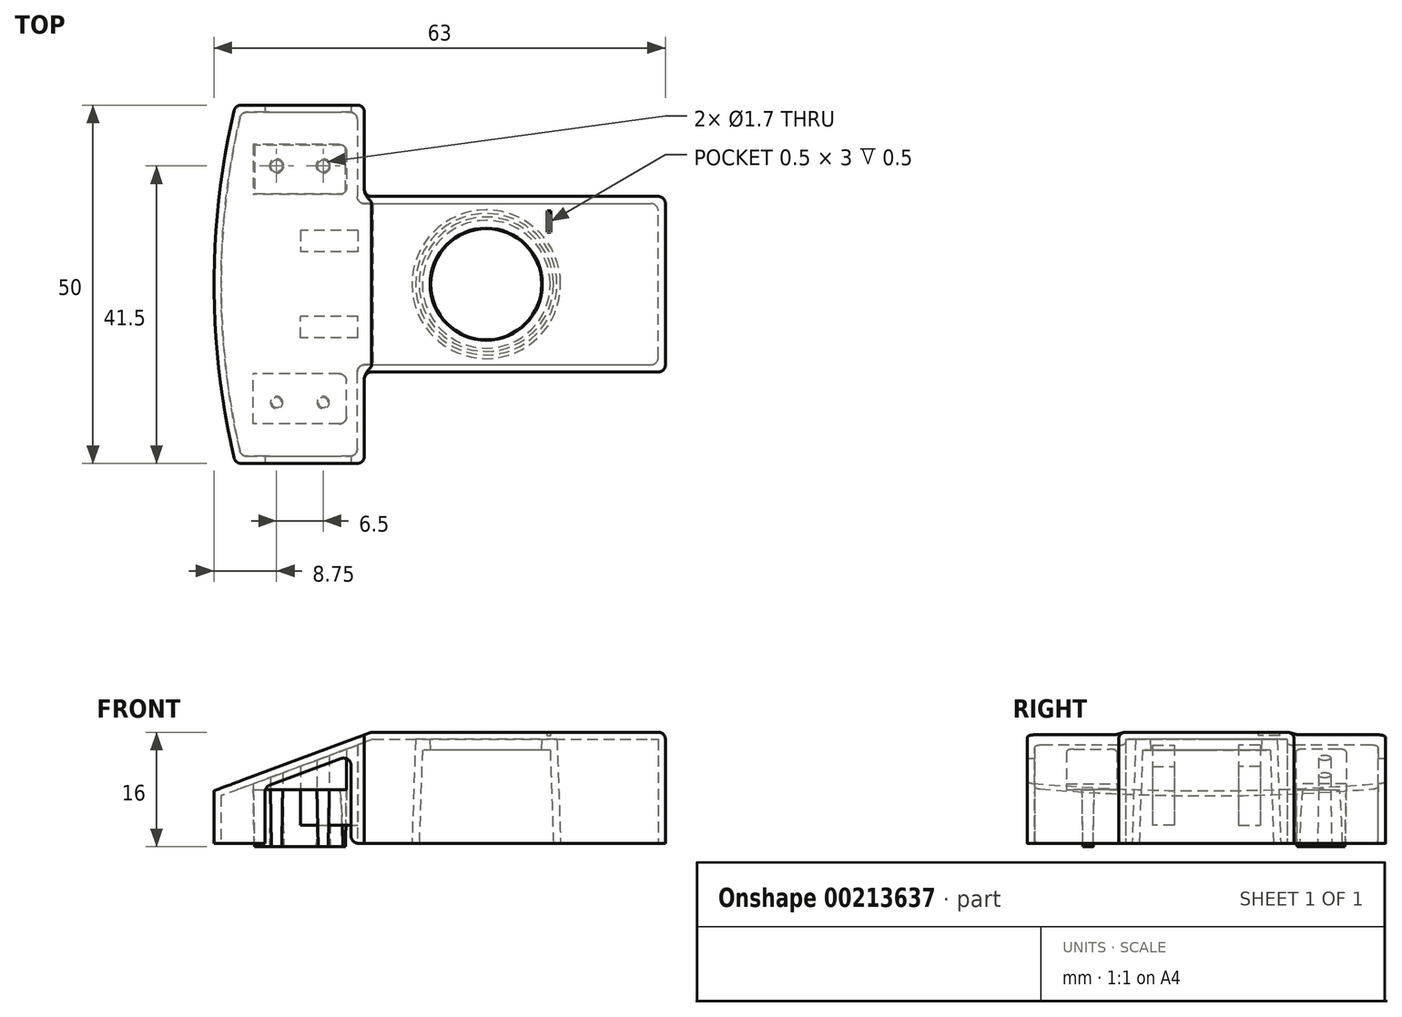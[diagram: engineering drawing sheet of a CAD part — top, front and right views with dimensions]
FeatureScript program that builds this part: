
annotation { "Feature Type Name" : "Feature", "Feature Type Description" : "" }
export const myFeature = defineFeature(function(context is Context, id is Id, definition is map)
    precondition{}
    {
        {
            var Q0;
            Q0=qCreatedBy(makeId("Top.planeOp"),FACE);
            var sketch = newSketch(context, id + "F0", { "sketchPlane" : qUnion([Q0])});
            skCircle(sketch, "E0", {"center": v(-4, 0) * mm, "radius": 9.37 * mm});
            skLineSegment(sketch, "E1.bottom", {"start": v(-21, -12.25) * mm, "end": v(21, -12.25) * mm});
            skLineSegment(sketch, "E1.top", {"start": v(-21, 12.25) * mm, "end": v(21, 12.25) * mm});
            skLineSegment(sketch, "E1.right", {"start": v(21, -12.25) * mm, "end": v(21, 12.25) * mm});
            skLineSegment(sketch, "E2.bottom", {"start": v(-21, -25) * mm, "end": v(-39, -25) * mm});
            skLineSegment(sketch, "E2.top", {"start": v(-21, 25) * mm, "end": v(-39, 25) * mm});
            skLineSegment(sketch, "E2.left", {"start": v(-21, -25) * mm, "end": v(-21, -12.25) * mm});
            skLineSegment(sketch, "E2.right", {"start": v(-39, -25) * mm, "end": v(-39, 25) * mm});
            skPoint(sketch, "E2.middle", {"position": v(-30, 0) * mm});
            skLineSegment(sketch, "E3.trimOffspring", {"start": v(-21, 12.25) * mm, "end": v(-21, 25) * mm});
            skLineSegment(sketch, "E4", {"start": v(-20, 12.25) * mm, "end": v(-20, -12.25) * mm});
            skPoint(sketch, "E5", {"position": v(-42, 0) * mm});
            skPoint(sketch, "E5.positionSnap0", {"position": v(-39, 0) * mm});
            skArc(sketch, "E6", {"start": v(-39, 25) * mm, "mid": v(-42, 0) * mm, "end": v(-39, -25) * mm});
            skSolve(sketch);
        }
        {
            var Q0;
            Q0=qSketchRegion(id+"F0",true);
            var Q1;
            Q1=makeQuery(id+"F0.imprint","IMPRINT",FACE,{"disambiguationData":[TD([[makeQuery(id+"F0.imprint","IMPRINT",EDGE,{"derivedFrom":sQuery(id+"F0.wireOp",EDGE,"E0")}),1.0]])]});
            extrude(context, id + "F1", {"entities" : qUnion([Q0, Q1]), "depth" : 15.5 * mm});
        }
        {
            var Q0;
            Q0=makeQuery(id+"F0.imprint","IMPRINT",FACE,{"disambiguationData":[TD([[makeQuery(id+"F0.imprint","IMPRINT",EDGE,{"derivedFrom":sQuery(id+"F0.wireOp",EDGE,"E0")}),1.0]])]});
            var Q1;
            Q1=makeQuery(id+"F1.opExtrude","CAP_FACE",FACE,{"disambiguationData":[OSD([sQuery(id+"F0.wireOp",EDGE,"E1.bottom"),sQuery(id+"F0.wireOp",EDGE,"E1.top"),sQuery(id+"F0.wireOp",EDGE,"E1.right"),sQuery(id+"F0.wireOp",EDGE,"E2.bottom"),sQuery(id+"F0.wireOp",EDGE,"E2.top"),sQuery(id+"F0.wireOp",EDGE,"E2.left"),sQuery(id+"F0.wireOp",EDGE,"E3.trimOffspring"),sQuery(id+"F0.wireOp",EDGE,"E6")])],"isStart":false});
            extrude(context, id + "F2", {"entities" : qUnion([Q0]), "operationType" : NewBodyOperationType.REMOVE, "endBound" : BoundingType.UP_TO_SURFACE, "endBoundEntityFace" : qUnion([Q1]), "depth" : 25 * mm, "hasDraft" : true, "draftAngle" : 2 * degree, "draftPullDirection" : true});
        }
        {
            var Q0;
            Q0=qCreatedBy(makeId("Front.planeOp"),FACE);
            var Q1;
            Q1=makeQuery(id+"F1.opExtrude","CAP_EDGE",EDGE,{"disambiguationData":[OSD([sQuery(id+"F0.wireOp",EDGE,"E2.bottom")])],"isStart":true});
            cPlane(context, id + "F3", {"entities" : qUnion([Q0, Q1]), "cplaneType" : CPlaneType.LINE_ANGLE, "offset" : 25 * mm, "angle" : 0 * degree, "width" : 150 * mm, "height" : 150 * mm});
        }
        {
            var Q0;
            Q0=qCreatedBy(id+"F3.planeOp",FACE);
            var sketch = newSketch(context, id + "F4", { "sketchPlane" : qUnion([Q0])});
            skLineSegment(sketch, "E7", {"start": v(20, 15.5) * mm, "end": v(42, 15.5) * mm});
            skLineSegment(sketch, "E8", {"start": v(42, 15.5) * mm, "end": v(42, 7.32) * mm});
            skLineSegment(sketch, "E9", {"start": v(42, 7.32) * mm, "end": v(20, 15.5) * mm});
            skLineSegment(sketch, "E10", {"start": v(42, 0) * mm, "end": v(41.46, 15.5) * mm, "construction": true});
            skLineSegment(sketch, "E11", {"start": v(42, 0) * mm, "end": v(42, 27.73) * mm, "construction": true});
            skSolve(sketch);
        }
        {
            var Q0;
            Q0=qSketchRegion(id+"F4",true);
            extrude(context, id + "F5", {"entities" : qUnion([Q0]), "operationType" : NewBodyOperationType.REMOVE, "endBound" : BoundingType.THROUGH_ALL, "depth" : 25 * mm});
        }
        {
            var Q0;
            Q0=makeQuery(id+"F1.opExtrude","CAP_FACE",FACE,{"disambiguationData":[OSD([sQuery(id+"F0.wireOp",EDGE,"E1.bottom"),sQuery(id+"F0.wireOp",EDGE,"E1.top"),sQuery(id+"F0.wireOp",EDGE,"E1.right"),sQuery(id+"F0.wireOp",EDGE,"E2.bottom"),sQuery(id+"F0.wireOp",EDGE,"E2.top"),sQuery(id+"F0.wireOp",EDGE,"E2.left"),sQuery(id+"F0.wireOp",EDGE,"E3.trimOffspring"),sQuery(id+"F0.wireOp",EDGE,"E6")])],"isStart":true});
            shell(context, id + "F6", {"entities" : qUnion([Q0]), "thickness" : 1 * mm});
        }
        {
            var Q0;
            Q0=makeQuery(id+"F1.opExtrude","SWEPT_FACE",FACE,{"disambiguationData":[OSD([sQuery(id+"F0.wireOp",EDGE,"E2.bottom")])]});
            var sketch = newSketch(context, id + "F7", { "sketchPlane" : qUnion([Q0])});
            skLineSegment(sketch, "E12", {"start": v(-20, 15.5) * mm, "end": v(-39, 8.43) * mm});
            skLineSegment(sketch, "E13", {"start": v(-39, 8.43) * mm, "end": v(-39, 15.5) * mm});
            skLineSegment(sketch, "E14", {"start": v(-39, 15.5) * mm, "end": v(-20, 15.5) * mm});
            skLineSegment(sketch, "E15", {"start": v(-34.87, 0) * mm, "end": v(-34.87, 7.86) * mm});
            skLineSegment(sketch, "E16", {"start": v(-34.87, 7.86) * mm, "end": v(-22.87, 12.32) * mm});
            skLineSegment(sketch, "E17", {"start": v(-22.87, 0) * mm, "end": v(-34.87, 0) * mm});
            skLineSegment(sketch, "E18", {"start": v(-22.87, 12.32) * mm, "end": v(-22.87, 0) * mm});
            skSolve(sketch);
        }
        {
            var Q0;
            Q0=makeQuery(id+"F7.imprint","IMPRINT",FACE,{"disambiguationData":[TD([[makeQuery(id+"F7.imprint","IMPRINT",EDGE,{"derivedFrom":sQuery(id+"F7.wireOp",EDGE,"E15")}),-1.0]])]});
            extrude(context, id + "F8", {"entities" : qUnion([Q0]), "operationType" : NewBodyOperationType.REMOVE, "endBound" : BoundingType.THROUGH_ALL, "oppositeDirection" : true, "depth" : 25 * mm});
        }
        {
            var Q0;
            Q0=makeQuery(id+"F1.opExtrude","CAP_FACE",FACE,{"disambiguationData":[OSD([sQuery(id+"F0.wireOp",EDGE,"E0"),sQuery(id+"F0.wireOp",EDGE,"E1.bottom"),sQuery(id+"F0.wireOp",EDGE,"E1.top"),sQuery(id+"F0.wireOp",EDGE,"E1.right"),sQuery(id+"F0.wireOp",EDGE,"E2.bottom"),sQuery(id+"F0.wireOp",EDGE,"E2.top"),sQuery(id+"F0.wireOp",EDGE,"E2.left"),sQuery(id+"F0.wireOp",EDGE,"E2.right"),sQuery(id+"F0.wireOp",EDGE,"E3.trimOffspring")])],"isStart":false});
            cPlane(context, id + "F9", {"entities" : qUnion([Q0]), "cplaneType" : CPlaneType.OFFSET, "offset" : 8 * mm, "oppositeDirection" : true, "width" : 150 * mm, "height" : 150 * mm});
        }
        {
            var Q0;
            Q0=qCreatedBy(id+"F9.planeOp",FACE);
            var sketch = newSketch(context, id + "F10", { "sketchPlane" : qUnion([Q0])});
            skLineSegment(sketch, "E19", {"start": v(0, 0) * mm, "end": v(-63, 0) * mm, "construction": true});
            skLineSegment(sketch, "E20.bottom", {"start": v(-36.5, -12.5) * mm, "end": v(-23.5, -12.5) * mm});
            skLineSegment(sketch, "E20.top", {"start": v(-36.5, -19.5) * mm, "end": v(-23.5, -19.5) * mm});
            skLineSegment(sketch, "E20.left", {"start": v(-36.5, -12.5) * mm, "end": v(-36.5, -19.5) * mm});
            skLineSegment(sketch, "E20.right", {"start": v(-23.5, -12.5) * mm, "end": v(-23.5, -19.5) * mm});
            skPoint(sketch, "E20.middle", {"position": v(-30, -16) * mm});
            skPoint(sketch, "E21", {"position": v(-33.25, -16.5) * mm});
            skPoint(sketch, "E22", {"position": v(-26.75, -16.5) * mm});
            skCircle(sketch, "E23", {"center": v(-33.25, -16.5) * mm, "radius": 0.85 * mm});
            skCircle(sketch, "E24", {"center": v(-26.75, -16.5) * mm, "radius": 0.85 * mm});
            skLineSegment(sketch, "E25.MirrorCS", {"start": v(-36.5, 12.5) * mm, "end": v(-23.5, 12.5) * mm});
            skLineSegment(sketch, "E26.MirrorCS", {"start": v(-36.5, 12.5) * mm, "end": v(-36.5, 19.5) * mm});
            skLineSegment(sketch, "E27.MirrorCS", {"start": v(-36.5, 19.5) * mm, "end": v(-23.5, 19.5) * mm});
            skLineSegment(sketch, "E28.MirrorCS", {"start": v(-23.5, 12.5) * mm, "end": v(-23.5, 19.5) * mm});
            skCircle(sketch, "E29.MirrorC", {"center": v(-26.75, 16.5) * mm, "radius": 0.85 * mm});
            skCircle(sketch, "E30.MirrorC", {"center": v(-33.25, 16.5) * mm, "radius": 0.85 * mm});
            skSolve(sketch);
        }
        {
            var Q0;
            Q0=makeQuery(id+"F10.imprint","IMPRINT",FACE,{"disambiguationData":[TD([[makeQuery(id+"F10.imprint","IMPRINT",EDGE,{"derivedFrom":sQuery(id+"F10.wireOp",EDGE,"E20.bottom")}),-1.0]])]});
            var Q1;
            Q1=makeQuery(id+"F10.imprint","IMPRINT",FACE,{"disambiguationData":[TD([[makeQuery(id+"F10.imprint","IMPRINT",EDGE,{"derivedFrom":sQuery(id+"F10.wireOp",EDGE,"E23")}),1.0]])]});
            var Q2;
            Q2=makeQuery(id+"F10.imprint","IMPRINT",FACE,{"disambiguationData":[TD([[makeQuery(id+"F10.imprint","IMPRINT",EDGE,{"derivedFrom":sQuery(id+"F10.wireOp",EDGE,"E24")}),1.0]])]});
            var Q3;
            Q3=makeQuery(id+"F10.imprint","IMPRINT",FACE,{"disambiguationData":[TD([[makeQuery(id+"F10.imprint","IMPRINT",EDGE,{"derivedFrom":sQuery(id+"F10.wireOp",EDGE,"E25.MirrorCS")}),1.0]])]});
            var Q4;
            Q4=makeQuery(id+"F10.imprint","IMPRINT",FACE,{"disambiguationData":[TD([[makeQuery(id+"F10.imprint","IMPRINT",EDGE,{"derivedFrom":sQuery(id+"F10.wireOp",EDGE,"E30.MirrorC")}),-1.0]])]});
            var Q5;
            Q5=makeQuery(id+"F10.imprint","IMPRINT",FACE,{"disambiguationData":[TD([[makeQuery(id+"F10.imprint","IMPRINT",EDGE,{"derivedFrom":sQuery(id+"F10.wireOp",EDGE,"E29.MirrorC")}),-1.0]])]});
            var Q6;
            Q6=makeQuery(id+"F6.opShell","OFFSET_FACE",FACE,{"disambiguationData":[OSD([sQuery(id+"F4.wireOp",EDGE,"E9")])]});
            extrude(context, id + "F11", {"entities" : qUnion([Q0, Q1, Q2, Q3, Q4, Q5]), "operationType" : NewBodyOperationType.ADD, "endBound" : BoundingType.UP_TO_SURFACE, "endBoundEntityFace" : qUnion([Q6]), "depth" : 25 * mm});
        }
        {
            var Q0;
            Q0=makeQuery(id+"F10.imprint","IMPRINT",FACE,{"disambiguationData":[TD([[makeQuery(id+"F10.imprint","IMPRINT",EDGE,{"derivedFrom":sQuery(id+"F10.wireOp",EDGE,"E23")}),1.0]])]});
            var Q1;
            Q1=makeQuery(id+"F10.imprint","IMPRINT",FACE,{"disambiguationData":[TD([[makeQuery(id+"F10.imprint","IMPRINT",EDGE,{"derivedFrom":sQuery(id+"F10.wireOp",EDGE,"E29.MirrorC")}),-1.0]])]});
            var Q2;
            Q2=makeQuery(id+"F10.imprint","IMPRINT",FACE,{"disambiguationData":[TD([[makeQuery(id+"F10.imprint","IMPRINT",EDGE,{"derivedFrom":sQuery(id+"F10.wireOp",EDGE,"E30.MirrorC")}),-1.0]])]});
            var Q3;
            Q3=makeQuery(id+"F10.imprint","IMPRINT",FACE,{"disambiguationData":[TD([[makeQuery(id+"F10.imprint","IMPRINT",EDGE,{"derivedFrom":sQuery(id+"F10.wireOp",EDGE,"E24")}),1.0]])]});
            extrude(context, id + "F12", {"entities" : qUnion([Q0, Q1, Q2, Q3]), "operationType" : NewBodyOperationType.ADD, "oppositeDirection" : true, "depth" : 8 * mm, "hasDraft" : true, "draftAngle" : 1 * degree, "draftPullDirection" : true});
        }
        {
            var Q0;
            Q0=makeQuery(id+"F1.opExtrude","CAP_EDGE",EDGE,{"disambiguationData":[OSD([sQuery(id+"F0.wireOp",EDGE,"E1.bottom")])],"isStart":false});
            var Q1;
            Q1=makeQuery(id+"F1.opExtrude","CAP_EDGE",EDGE,{"disambiguationData":[OSD([sQuery(id+"F0.wireOp",EDGE,"E1.right")])],"isStart":false});
            var Q2;
            Q2=makeQuery(id+"F1.opExtrude","CAP_EDGE",EDGE,{"disambiguationData":[OSD([sQuery(id+"F0.wireOp",EDGE,"E1.top")])],"isStart":false});
            var Q3;
            Q3=makeQuery(id+"F1.opExtrude","SWEPT_EDGE",EDGE,{"disambiguationData":[OSD([sQuery(id+"F0.wireOp",EDGE,"E1.bottom"),sQuery(id+"F0.wireOp",EDGE,"E1.right")])]});
            var Q4;
            Q4=makeQuery(id+"F1.opExtrude","SWEPT_EDGE",EDGE,{"disambiguationData":[OSD([sQuery(id+"F0.wireOp",EDGE,"E1.top"),sQuery(id+"F0.wireOp",EDGE,"E1.right")])]});
            fillet(context, id + "F13", {"entities" : qUnion([Q0, Q1, Q2, Q3, Q4]), "radius" : 1 * mm, "tangentPropagation" : true, "allowEdgeOverflow" : false});
        }
        {
            var Q0;
            Q0=makeQuery(id+"F1.opExtrude","SWEPT_EDGE",EDGE,{"disambiguationData":[OSD([sQuery(id+"F0.wireOp",EDGE,"E2.bottom"),sQuery(id+"F0.wireOp",EDGE,"E2.left")])]});
            var Q1;
            Q1=makeQuery(id+"F5.boolean.opBoolean","INTERSECT",EDGE,{"derivedFrom":[makeQuery(id+"F1.opExtrude","SWEPT_FACE",FACE,{"disambiguationData":[OSD([sQuery(id+"F0.wireOp",EDGE,"E2.left")])]}),makeQuery(id+"F5.opExtrude","SWEPT_FACE",FACE,{"disambiguationData":[OSD([sQuery(id+"FjstzwEYRuGCUyq_1.wireOp",EDGE,"6156deb2-2619-4c56-9df6-34b3699534c4")])]})]});
            var Q2;
            Q2=makeQuery(id+"F5.boolean.opBoolean","COPY",EDGE,{"derivedFrom":makeQuery(id+"F5.opExtrude","CAP_EDGE",EDGE,{"disambiguationData":[OSD([sQuery(id+"FjstzwEYRuGCUyq_1.wireOp",EDGE,"6156deb2-2619-4c56-9df6-34b3699534c4")])],"isStart":true})});
            var Q3;
            Q3=makeQuery(id+"F1.opExtrude","SWEPT_EDGE",EDGE,{"disambiguationData":[OSD([sQuery(id+"F0.wireOp",EDGE,"E2.bottom"),sQuery(id+"F0.wireOp",EDGE,"E2.right"),sQuery(id+"F0.wireOp",EDGE,"E6")])]});
            var Q4;
            Q4=makeQuery(id+"F5.boolean.opBoolean","INTERSECT",EDGE,{"derivedFrom":[makeQuery(id+"F1.opExtrude","SWEPT_FACE",FACE,{"disambiguationData":[OSD([sQuery(id+"F0.wireOp",EDGE,"E6")])]}),makeQuery(id+"F5.opExtrude","SWEPT_FACE",FACE,{"disambiguationData":[OSD([sQuery(id+"FjstzwEYRuGCUyq_1.wireOp",EDGE,"6156deb2-2619-4c56-9df6-34b3699534c4")])]})]});
            var Q5;
            Q5=makeQuery(id+"F5.boolean.opBoolean","INTERSECT",EDGE,{"derivedFrom":[makeQuery(id+"F1.opExtrude","SWEPT_FACE",FACE,{"disambiguationData":[OSD([sQuery(id+"F0.wireOp",EDGE,"E2.top")])]}),makeQuery(id+"F5.opExtrude","SWEPT_FACE",FACE,{"disambiguationData":[OSD([sQuery(id+"FjstzwEYRuGCUyq_1.wireOp",EDGE,"6156deb2-2619-4c56-9df6-34b3699534c4")])]})]});
            var Q6;
            Q6=makeQuery(id+"F1.opExtrude","SWEPT_EDGE",EDGE,{"disambiguationData":[OSD([sQuery(id+"F0.wireOp",EDGE,"E2.top"),sQuery(id+"F0.wireOp",EDGE,"E2.right"),sQuery(id+"F0.wireOp",EDGE,"E6")])]});
            var Q7;
            Q7=makeQuery(id+"F1.opExtrude","SWEPT_EDGE",EDGE,{"disambiguationData":[OSD([sQuery(id+"F0.wireOp",EDGE,"E2.top"),sQuery(id+"F0.wireOp",EDGE,"E3.trimOffspring")])]});
            var Q8;
            Q8=makeQuery(id+"F5.boolean.opBoolean","INTERSECT",EDGE,{"derivedFrom":[makeQuery(id+"F1.opExtrude","SWEPT_FACE",FACE,{"disambiguationData":[OSD([sQuery(id+"F0.wireOp",EDGE,"E3.trimOffspring")])]}),makeQuery(id+"F5.opExtrude","SWEPT_FACE",FACE,{"disambiguationData":[OSD([sQuery(id+"FjstzwEYRuGCUyq_1.wireOp",EDGE,"6156deb2-2619-4c56-9df6-34b3699534c4")])]})]});
            fillet(context, id + "F14", {"entities" : qUnion([Q0, Q1, Q2, Q3, Q4, Q5, Q6, Q7, Q8]), "radius" : 1 * mm, "tangentPropagation" : true, "allowEdgeOverflow" : false});
        }
        {
            var Q0;
            Q0=makeQuery(id+"F1.opExtrude","SWEPT_EDGE",EDGE,{"disambiguationData":[OSD([sQuery(id+"F0.wireOp",EDGE,"E1.top"),sQuery(id+"F0.wireOp",EDGE,"E3.trimOffspring")])]});
            fillet(context, id + "F15", {"entities" : qUnion([Q0]), "radius" : 1 * mm, "tangentPropagation" : true, "allowEdgeOverflow" : false});
        }
        {
            var Q0;
            Q0=makeQuery(id+"F1.opExtrude","SWEPT_EDGE",EDGE,{"disambiguationData":[OSD([sQuery(id+"F0.wireOp",EDGE,"E1.bottom"),sQuery(id+"F0.wireOp",EDGE,"E2.left")])]});
            var Q1;
            {var subQ0=sQuery(id+"F0.wireOp",EDGE,"E2.bottom");var subQ1=sQuery(id+"F7.wireOp",EDGE,"E18");Q1=makeQuery(id+"F8.boolean.opBoolean","COPY",EDGE,{"disambiguationData":[TD([makeQuery(id+"F1.opExtrude","SWEPT_FACE",FACE,{"disambiguationData":[OSD([subQ0])]})])],"derivedFrom":makeQuery(id+"F8.opExtrude","SWEPT_EDGE",EDGE,{"disambiguationData":[OSD([subQ0,sQuery(id+"F7.wireOp",EDGE,"E17"),subQ1])]})});}
            var Q2;
            {var subQ0=sQuery(id+"F0.wireOp",EDGE,"E2.bottom");var subQ1=sQuery(id+"F7.wireOp",EDGE,"E15");Q2=makeQuery(id+"F8.boolean.opBoolean","COPY",EDGE,{"disambiguationData":[TD([makeQuery(id+"F1.opExtrude","SWEPT_FACE",FACE,{"disambiguationData":[OSD([subQ0])]})])],"derivedFrom":makeQuery(id+"F8.opExtrude","SWEPT_EDGE",EDGE,{"disambiguationData":[OSD([subQ0,subQ1,sQuery(id+"F7.wireOp",EDGE,"E17")])]})});}
            var Q3;
            {var subQ0=sQuery(id+"F0.wireOp",EDGE,"E2.top");var subQ1=sQuery(id+"F0.wireOp",EDGE,"E2.bottom");var subQ2=sQuery(id+"F7.wireOp",EDGE,"E15");Q3=makeQuery(id+"F8.boolean.opBoolean","COPY",EDGE,{"disambiguationData":[TD([makeQuery(id+"F1.opExtrude","SWEPT_FACE",FACE,{"disambiguationData":[OSD([subQ0])]})])],"derivedFrom":makeQuery(id+"F8.opExtrude","SWEPT_EDGE",EDGE,{"disambiguationData":[OSD([subQ1,subQ2,sQuery(id+"F7.wireOp",EDGE,"E17")])]})});}
            var Q4;
            {var subQ0=sQuery(id+"F0.wireOp",EDGE,"E2.top");var subQ1=sQuery(id+"F0.wireOp",EDGE,"E2.bottom");var subQ2=sQuery(id+"F7.wireOp",EDGE,"E18");Q4=makeQuery(id+"F8.boolean.opBoolean","COPY",EDGE,{"disambiguationData":[TD([makeQuery(id+"F1.opExtrude","SWEPT_FACE",FACE,{"disambiguationData":[OSD([subQ0])]})])],"derivedFrom":makeQuery(id+"F8.opExtrude","SWEPT_EDGE",EDGE,{"disambiguationData":[OSD([subQ1,sQuery(id+"F7.wireOp",EDGE,"E17"),subQ2])]})});}
            var Q5;
            {var subQ0=sQuery(id+"F0.wireOp",EDGE,"E2.top");var subQ1=sQuery(id+"F7.wireOp",EDGE,"E18");var subQ2=sQuery(id+"F7.wireOp",EDGE,"E16");Q5=makeQuery(id+"F8.boolean.opBoolean","COPY",EDGE,{"disambiguationData":[TD([makeQuery(id+"F1.opExtrude","SWEPT_FACE",FACE,{"disambiguationData":[OSD([subQ0])]})])],"derivedFrom":makeQuery(id+"F8.opExtrude","SWEPT_EDGE",EDGE,{"disambiguationData":[OSD([subQ2,subQ1])]})});}
            var Q6;
            {var subQ0=sQuery(id+"F0.wireOp",EDGE,"E2.top");var subQ1=sQuery(id+"F7.wireOp",EDGE,"E15");var subQ2=sQuery(id+"F7.wireOp",EDGE,"E16");Q6=makeQuery(id+"F8.boolean.opBoolean","COPY",EDGE,{"disambiguationData":[TD([makeQuery(id+"F1.opExtrude","SWEPT_FACE",FACE,{"disambiguationData":[OSD([subQ0])]})])],"derivedFrom":makeQuery(id+"F8.opExtrude","SWEPT_EDGE",EDGE,{"disambiguationData":[OSD([subQ1,subQ2])]})});}
            var Q7;
            {var subQ0=sQuery(id+"F0.wireOp",EDGE,"E2.bottom");var subQ1=sQuery(id+"F7.wireOp",EDGE,"E18");var subQ2=sQuery(id+"F7.wireOp",EDGE,"E16");Q7=makeQuery(id+"F8.boolean.opBoolean","COPY",EDGE,{"disambiguationData":[TD([makeQuery(id+"F1.opExtrude","SWEPT_FACE",FACE,{"disambiguationData":[OSD([subQ0])]})])],"derivedFrom":makeQuery(id+"F8.opExtrude","SWEPT_EDGE",EDGE,{"disambiguationData":[OSD([subQ2,subQ1])]})});}
            var Q8;
            {var subQ0=sQuery(id+"F0.wireOp",EDGE,"E2.bottom");var subQ1=sQuery(id+"F7.wireOp",EDGE,"E15");var subQ2=sQuery(id+"F7.wireOp",EDGE,"E16");Q8=makeQuery(id+"F8.boolean.opBoolean","COPY",EDGE,{"disambiguationData":[TD([makeQuery(id+"F1.opExtrude","SWEPT_FACE",FACE,{"disambiguationData":[OSD([subQ0])]})])],"derivedFrom":makeQuery(id+"F8.opExtrude","SWEPT_EDGE",EDGE,{"disambiguationData":[OSD([subQ1,subQ2])]})});}
            var Q9;
            Q9=makeQuery(id+"F6.opShell","OFFSET_EDGE",EDGE,{"disambiguationData":[OSD([sQuery(id+"F0.wireOp",EDGE,"E1.top"),sQuery(id+"F0.wireOp",EDGE,"E3.trimOffspring")])]});
            var Q10;
            Q10=makeQuery(id+"F6.opShell","OFFSET_EDGE",EDGE,{"disambiguationData":[OSD([sQuery(id+"F0.wireOp",EDGE,"E1.bottom"),sQuery(id+"F0.wireOp",EDGE,"E2.left")])]});
            fillet(context, id + "F16", {"entities" : qUnion([Q0, Q1, Q2, Q3, Q4, Q5, Q6, Q7, Q8, Q9, Q10]), "radius" : 1 * mm, "tangentPropagation" : true, "allowEdgeOverflow" : false});
        }
        {
            var Q0;
            Q0=makeQuery(id+"F6.opShell","OFFSET_EDGE",EDGE,{"disambiguationData":[OSD([sQuery(id+"F0.wireOp",EDGE,"E1.top"),sQuery(id+"F0.wireOp",EDGE,"E1.right")])]});
            var Q1;
            Q1=makeQuery(id+"F6.opShell","OFFSET_EDGE",EDGE,{"disambiguationData":[OSD([sQuery(id+"F0.wireOp",EDGE,"E1.bottom"),sQuery(id+"F0.wireOp",EDGE,"E1.right")])]});
            var Q2;
            {var subQ0=sQuery(id+"F0.wireOp",EDGE,"E0");Q2=makeQuery(id+"F6.opShell","OFFSET_EDGE",EDGE,{"disambiguationData":[OSD([subQ0]),TDD([makeQuery(id+"F1.opExtrude","CAP_EDGE",EDGE,{"disambiguationData":[OSD([subQ0])],"isStart":false})])]});}
            var Q3;
            Q3=makeQuery(id+"F6.opShell","OFFSET_EDGE",EDGE,{"disambiguationData":[OSD([sQuery(id+"F0.wireOp",EDGE,"E2.top"),sQuery(id+"F0.wireOp",EDGE,"E3.trimOffspring")])]});
            var Q4;
            Q4=makeQuery(id+"F6.opShell","OFFSET_EDGE",EDGE,{"disambiguationData":[OSD([sQuery(id+"F0.wireOp",EDGE,"E2.top"),sQuery(id+"F0.wireOp",EDGE,"E2.right"),sQuery(id+"F0.wireOp",EDGE,"E6")])]});
            var Q5;
            Q5=makeQuery(id+"F6.opShell","OFFSET_EDGE",EDGE,{"disambiguationData":[OSD([sQuery(id+"F0.wireOp",EDGE,"E2.bottom"),sQuery(id+"F0.wireOp",EDGE,"E2.left")])]});
            var Q6;
            Q6=makeQuery(id+"F6.opShell","OFFSET_EDGE",EDGE,{"disambiguationData":[OSD([sQuery(id+"F0.wireOp",EDGE,"E2.bottom"),sQuery(id+"F0.wireOp",EDGE,"E2.right"),sQuery(id+"F0.wireOp",EDGE,"E6")])]});
            var Q7;
            Q7=makeQuery(id+"F11.opExtrude","SWEPT_EDGE",EDGE,{"disambiguationData":[OSD([sQuery(id+"F10.wireOp",EDGE,"E20.bottom"),sQuery(id+"F10.wireOp",EDGE,"E20.right")])]});
            var Q8;
            Q8=makeQuery(id+"F11.opExtrude","SWEPT_EDGE",EDGE,{"disambiguationData":[OSD([sQuery(id+"F10.wireOp",EDGE,"E20.top"),sQuery(id+"F10.wireOp",EDGE,"E20.right")])]});
            var Q9;
            Q9=makeQuery(id+"F11.opExtrude","SWEPT_EDGE",EDGE,{"disambiguationData":[OSD([sQuery(id+"F10.wireOp",EDGE,"E27.MirrorCS"),sQuery(id+"F10.wireOp",EDGE,"E28.MirrorCS")])]});
            var Q10;
            Q10=makeQuery(id+"F11.opExtrude","SWEPT_EDGE",EDGE,{"disambiguationData":[OSD([sQuery(id+"F10.wireOp",EDGE,"E25.MirrorCS"),sQuery(id+"F10.wireOp",EDGE,"E28.MirrorCS")])]});
            fillet(context, id + "F17", {"entities" : qUnion([Q0, Q1, Q2, Q3, Q4, Q5, Q6, Q7, Q8, Q9, Q10]), "radius" : 1 * mm, "tangentPropagation" : true, "allowEdgeOverflow" : false});
        }
        {
            var Q0;
            Q0=qCreatedBy(id+"F9.planeOp",FACE);
            var sketch = newSketch(context, id + "F18", { "sketchPlane" : qUnion([Q0])});
            skPoint(sketch, "E31", {"position": v(-29.94, -4.5) * mm});
            skLineSegment(sketch, "E32.bottom", {"start": v(-29.94, -4.5) * mm, "end": v(-21.94, -4.5) * mm});
            skLineSegment(sketch, "E32.top", {"start": v(-29.94, -7.5) * mm, "end": v(-21.94, -7.5) * mm});
            skLineSegment(sketch, "E32.left", {"start": v(-29.94, -4.5) * mm, "end": v(-29.94, -7.5) * mm});
            skLineSegment(sketch, "E32.right", {"start": v(-21.94, -4.5) * mm, "end": v(-21.94, -7.5) * mm});
            skLineSegment(sketch, "E33", {"start": v(0, 0) * mm, "end": v(-48.4, 0) * mm, "construction": true});
            skLineSegment(sketch, "E34.MirrorCS", {"start": v(-29.94, 4.5) * mm, "end": v(-21.94, 4.5) * mm});
            skLineSegment(sketch, "E35.MirrorCS", {"start": v(-21.94, 4.5) * mm, "end": v(-21.94, 7.5) * mm});
            skLineSegment(sketch, "E36.MirrorCS", {"start": v(-29.94, 7.5) * mm, "end": v(-21.94, 7.5) * mm});
            skLineSegment(sketch, "E37.MirrorCS", {"start": v(-29.94, 4.5) * mm, "end": v(-29.94, 7.5) * mm});
            skSolve(sketch);
        }
        {
            var Q0;
            Q0=qSketchRegion(id+"F18",true);
            var Q1;
            Q1=makeQuery(id+"F6.opShell","OFFSET_FACE",FACE,{"disambiguationData":[OSD([sQuery(id+"F4.wireOp",EDGE,"E9")])]});
            extrude(context, id + "F19", {"entities" : qUnion([Q0]), "operationType" : NewBodyOperationType.ADD, "endBound" : BoundingType.UP_TO_SURFACE, "endBoundEntityFace" : qUnion([Q1]), "depth" : 25 * mm, "hasSecondDirection" : true, "secondDirectionOppositeDirection" : true, "secondDirectionDepth" : 5 * mm});
        }
        {
            var Q0;
            Q0=makeQuery(id+"F1.opExtrude","CAP_FACE",FACE,{"disambiguationData":[OSD([sQuery(id+"F0.wireOp",EDGE,"E1.bottom"),sQuery(id+"F0.wireOp",EDGE,"E1.top"),sQuery(id+"F0.wireOp",EDGE,"E1.right"),sQuery(id+"F0.wireOp",EDGE,"E2.bottom"),sQuery(id+"F0.wireOp",EDGE,"E2.top"),sQuery(id+"F0.wireOp",EDGE,"E2.left"),sQuery(id+"F0.wireOp",EDGE,"E3.trimOffspring"),sQuery(id+"F0.wireOp",EDGE,"E6")])],"isStart":false});
            var sketch = newSketch(context, id + "F20", { "sketchPlane" : qUnion([Q0])});
            skCircle(sketch, "E38", {"center": v(-4, 0) * mm, "radius": 8.83 * mm});
            skCircle(sketch, "E39.0", {"center": v(-4, 0) * mm, "radius": 7.83 * mm});
            skSolve(sketch);
        }
        {
            var Q0;
            Q0=makeQuery(id+"F20.imprint","IMPRINT",FACE,{"disambiguationData":[TD([[makeQuery(id+"F20.imprint","IMPRINT",EDGE,{"derivedFrom":sQuery(id+"F20.wireOp",EDGE,"E38")}),1.0]])]});
            extrude(context, id + "F21", {"entities" : qUnion([Q0]), "operationType" : NewBodyOperationType.ADD, "oppositeDirection" : true, "depth" : 2.5 * mm, "hasDraft" : true, "draftAngle" : 2 * degree});
        }
        {
            var Q0;
            Q0=makeQuery(id+"F21.boolean.opBoolean","MERGE",FACE,{"derivedFrom":[makeQuery(id+"F1.opExtrude","CAP_FACE",FACE,{"disambiguationData":[OSD([sQuery(id+"F0.wireOp",EDGE,"E1.bottom"),sQuery(id+"F0.wireOp",EDGE,"E1.top"),sQuery(id+"F0.wireOp",EDGE,"E1.right"),sQuery(id+"F0.wireOp",EDGE,"E2.bottom"),sQuery(id+"F0.wireOp",EDGE,"E2.top"),sQuery(id+"F0.wireOp",EDGE,"E2.left"),sQuery(id+"F0.wireOp",EDGE,"E3.trimOffspring"),sQuery(id+"F0.wireOp",EDGE,"E6")])],"isStart":false}),makeQuery(id+"F21.opExtrude","CAP_FACE",FACE,{"disambiguationData":[OSD([sQuery(id+"F20.wireOp",EDGE,"E38"),sQuery(id+"F20.wireOp",EDGE,"E39.0")])],"isStart":true})]});
            var sketch = newSketch(context, id + "F22", { "sketchPlane" : qUnion([Q0])});
            skLineSegment(sketch, "E40.bottom", {"start": v(4.5, 10.25) * mm, "end": v(5, 10.25) * mm});
            skLineSegment(sketch, "E40.top", {"start": v(4.5, 7.25) * mm, "end": v(5, 7.25) * mm});
            skLineSegment(sketch, "E40.left", {"start": v(4.5, 10.25) * mm, "end": v(4.5, 7.25) * mm});
            skLineSegment(sketch, "E40.right", {"start": v(5, 10.25) * mm, "end": v(5, 7.25) * mm});
            skSolve(sketch);
        }
        {
            var Q0;
            Q0 = qSketchRegion(id + "F22", true);
            extrude(context, id + "F23", {"entities" : qUnion([Q0]), "operationType" : NewBodyOperationType.REMOVE, "oppositeDirection" : true, "depth" : 0.5 * mm});
        }
    });
